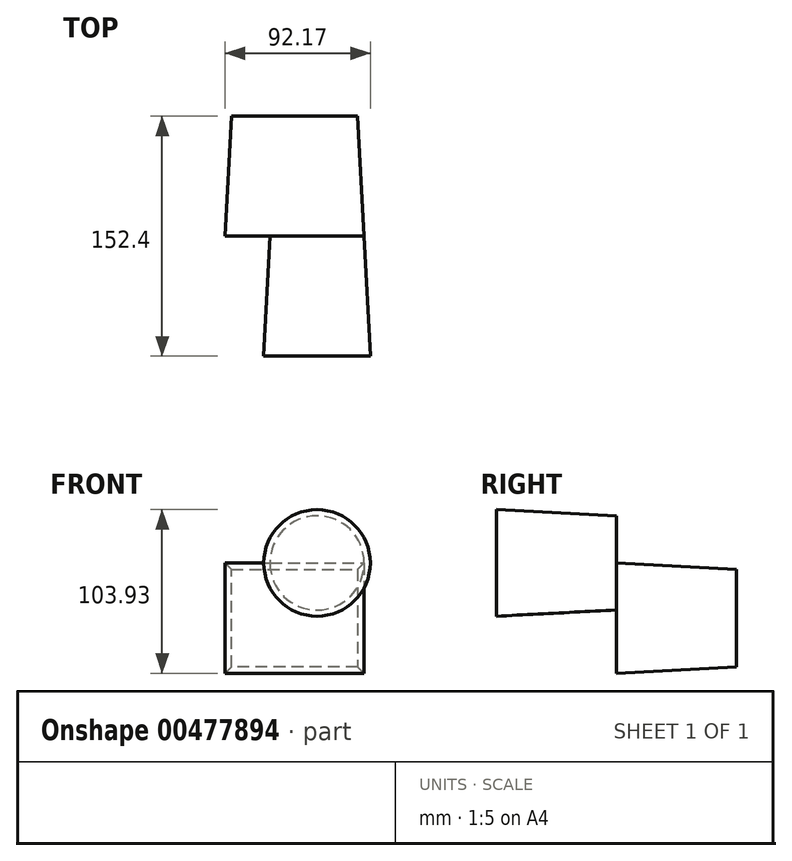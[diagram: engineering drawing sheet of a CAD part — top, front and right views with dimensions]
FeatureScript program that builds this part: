
annotation { "Feature Type Name" : "Feature", "Feature Type Description" : "" }
export const myFeature = defineFeature(function(context is Context, id is Id, definition is map)
    precondition{}
    {
        {
            var Q0;
            Q0=qCreatedBy(makeId("Front.planeOp"),FACE);
            var sketch = newSketch(context, id + "F0", { "sketchPlane" : qUnion([Q0])});
            skLineSegment(sketch, "E0", {"start": v(57.65, 32.15) * mm, "end": v(57.65, -29.93) * mm});
            skLineSegment(sketch, "E1", {"start": v(57.65, -29.93) * mm, "end": v(-22.54, -29.93) * mm});
            skLineSegment(sketch, "E2", {"start": v(-22.54, -29.93) * mm, "end": v(-22.54, 32.15) * mm});
            skLineSegment(sketch, "E3", {"start": v(57.65, 32.15) * mm, "end": v(-22.54, 32.15) * mm});
            skSolve(sketch);
        }
        {
            var Q0;
            Q0 = qSketchRegion(id + "F0", true);
            extrude(context, id + "F1", {"entities" : qUnion([Q0]), "depth" : 76.2 * mm, "hasDraft" : true, "draftAngle" : 3 * degree});
        }
        {
            var Q0;
            Q0=makeQuery(id+"F1.opExtrude","CAP_FACE",FACE,{"disambiguationData":[OSD([sQuery(id+"F0.wireOp",EDGE,"E0"),sQuery(id+"F0.wireOp",EDGE,"E1"),sQuery(id+"F0.wireOp",EDGE,"E2"),sQuery(id+"F0.wireOp",EDGE,"E3")])],"isStart":false});
            var sketch = newSketch(context, id + "F2", { "sketchPlane" : qUnion([Q0])});
            skCircle(sketch, "E4", {"center": v(31.78, 36.14) * mm, "radius": 29.86 * mm});
            skSolve(sketch);
        }
        {
            var Q0;
            Q0 = qSketchRegion(id + "F2", true);
            extrude(context, id + "F3", {"entities" : qUnion([Q0]), "operationType" : NewBodyOperationType.ADD, "depth" : 76.2 * mm, "hasDraft" : true, "draftAngle" : 3 * degree});
        }
    });
